# Revit family: ElectricalFixture_WiringAccessories_Hager_Sollyster_SwitchDimmers
name_source: partatom
category: Lighting Fixtures
revit_build: Autodesk Revit 2015 (Build: 20160512_1515(x64)
units: mm (PartAtom-declared; Revit-internal decimal feet)

## types (4) — shared parameters
CE Approval = Yes
Colour = SollystaWhite
Default Elevation = 1219.2 mm  [stored 4 ft]
Design Country = China
Expected Life = 25 years
Extrusion From Wall = 11.9 mm
Finish = Gloss
Frequency = 50/60Hz
Gross Weight kg = 0.165
LED Indicator Switch = No
Manufacturer = Hager
Manufacturer Country = United Kingdom
Manufacturer Website = http://www.hager.co.uk
Material = Urea Formaldehyde Thermoset Plastic
Overall Depth = 26.1 mm
Overall Height = 86 mm  [stored 0.282152 ft]
Packaging Recyclable = Yes
Product Family = WhiteMouldedDimmers_SwitchDimmers
Product Group = WiringAccessories
Product Literature = http://www.hager.co.uk
Product Range = Sollysta
Product URL = http://www.hager.co.uk
Reference Standard = BS 1363-2
Shape = Rectangular
Shipping Weight kg = 0.188
Supply Phase = 1
Switch = No
Type = ElectricalFixture
Voltage (Volts) = 230V/240V
zero-valued in all types: Overall Width

## per-type parameters (varying)
| type | 1 Gang | 2 Gang | 3 Gang | 4 Gang | Description | EAN Code | Features | Name | Overall Length | Technical Description |
| WMDS1 | Yes | No | No | No | 1GangDimmer400W | 5015654792961 | 1GangDimmer400W | WhiteMouldedDimmers_WMDS1 | 86 mm  [stored 0.282152 ft] | 1GangDimmer400W |
| WMDS2 | No | Yes | No | No | 2GangDimmer250W | 5015654792954 | 2GangDimmer250W | WhiteMouldedDimmers_WMDS2 | 86 mm  [stored 0.282152 ft] | 2GangDimmer250W |
| WMDS3 | Yes | No | Yes | No | 3GangDimmer250W | 5015654792978 | 3GangDimmer250W | WhiteMouldedDimmers_WMDS3 | 146 mm  [stored 0.479003 ft] | 3GangDimmer250W |
| WMDS4 | No | Yes | No | Yes | 4GangDimmer250W | 5015654792985 | 4GangDimmer250W | WhiteMouldedDimmers_WMDS4 | 146 mm  [stored 0.479003 ft] | 4GangDimmer250W |

note: column(s) folded — value = type name in every type: Product Model Number, Unique Reference

note: [stored X ft] marks values corroborated as IEEE doubles in the binary element streams (Revit-internal decimal feet)

## geometry (parser evidence)
native form markers: Blend x4, Sweep x8
no freeform markers — native parametric forms only
